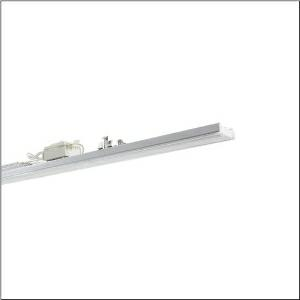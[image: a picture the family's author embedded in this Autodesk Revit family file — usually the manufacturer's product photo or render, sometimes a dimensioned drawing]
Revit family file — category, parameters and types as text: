
# Revit family: licross_11_recessed_mo_51tl14mn49xg
name_source: partatom
category: Lighting Fixtures
units: mm (PartAtom-declared; Revit-internal decimal feet)

## family parameters
Cut with Voids When Loaded = No
Host = Face
Light Source = No
Part Type = Normal
Room Calculation Point = No
Round Connector Dimension = Use Diameter
Shared = No

## types (1)
- --- (1 x LED, 9470 lm, 55.2 W, 4000K)
    Apparent Load = 55 VA
    CIE Flux Codes = 56 84 97 100 100
    Color Rendering = 80
    Color Temperature = 4000K
    Default Elevation = 1800 mm
    Description = Licross 11 Recessed MO, luminaire insert, of sheet steel, coil coated, white, length: 1.500mm, width: 66mm, height: 67mm, LED rated luminous flux: 9.470lm, light colour: 840, SDCM (Standard Deviation of Colour Matching)MacAdam ≤ 2 SDCM (initial), control gear: ON/OFF Multilumen, with plug, 3-pole, with phase selection, mains connection: 220..240V, AC, 50/60Hz, rated input power: 55W, internal wiring halogen-free, primary light control with lens, of plastic, primary optical cover: cover, of PMMA, light emission: direct distribution, primary light characteristic: asymmetric, protection rating (complete): IP40, insulation class (complete): insulation class I (protective earthing), certification: CE, ENEC, VDE, UKCA, protection symbol: D if used in an environment without relevant dust loads with corresponding accessories, impact resistance: IK06, permissible ambient temperature for indoor applications: -35..+40°C, corresponds to IFS (International Featured Standards) requirements for safety and quality in the food industry, reducing of maximum allowable ambient temperature of 5°C with ceiling mounting, The light source and the operating device comply with the requirements of the Ecodesign Regulation (EU) 2019/2020 and are replaceable in accordance with this regulation, packaging unit: 1 piece
    Height = 58 mm
    Lamp = 1 x LED
    Lamp Light Flux = 9470 lm
    Lamp Power = 55.2 W
    Lamp count = 1
    Length = 1500 mm
    Luminous efficacy = 172 lm/W
    Manufacturer = Siteco
    ModVariant = No
    Model = 51TL14MN49XG
    Mounting Place = Ceiling
    Mounting Type = Pendant
    Number of Poles = 1
    OnlyDefault = Yes
    Power Factor = 1
    Product Name = Licross 11 Recessed MO
    Product group = luminaire insert | ceiling pendant
    ProductGroupID = 901
    Protection Class = Protection class I
    Protection Degree = IP 40
    RLX_Detail_Level = 1
    RLX_Emergency_Light_Flux = 0 lm
    RLX_Emergency_Type = 0
    RLX_Emergency_Type_DB = No
    RlxData = <blob elided: 22929 chars, md5=5d250397>
    Socket = socket
    Standby Power = 0 W
    System Light Flux = 9470 lm
    System Power = 55 W
    Type Comments = factory setting: luminous flux: 100 % | (A | C | E) | 126 mA
    Type Image = l_1296930.jpg
    URL = http://relux.com
    VarID = @adj_089999
    Voltage = 0 V
    Weight = 0.00 kg
    Width = 66 mm

## geometry (parser evidence)
native form markers: Blend x4, Sweep x12
no freeform markers — native parametric forms only
